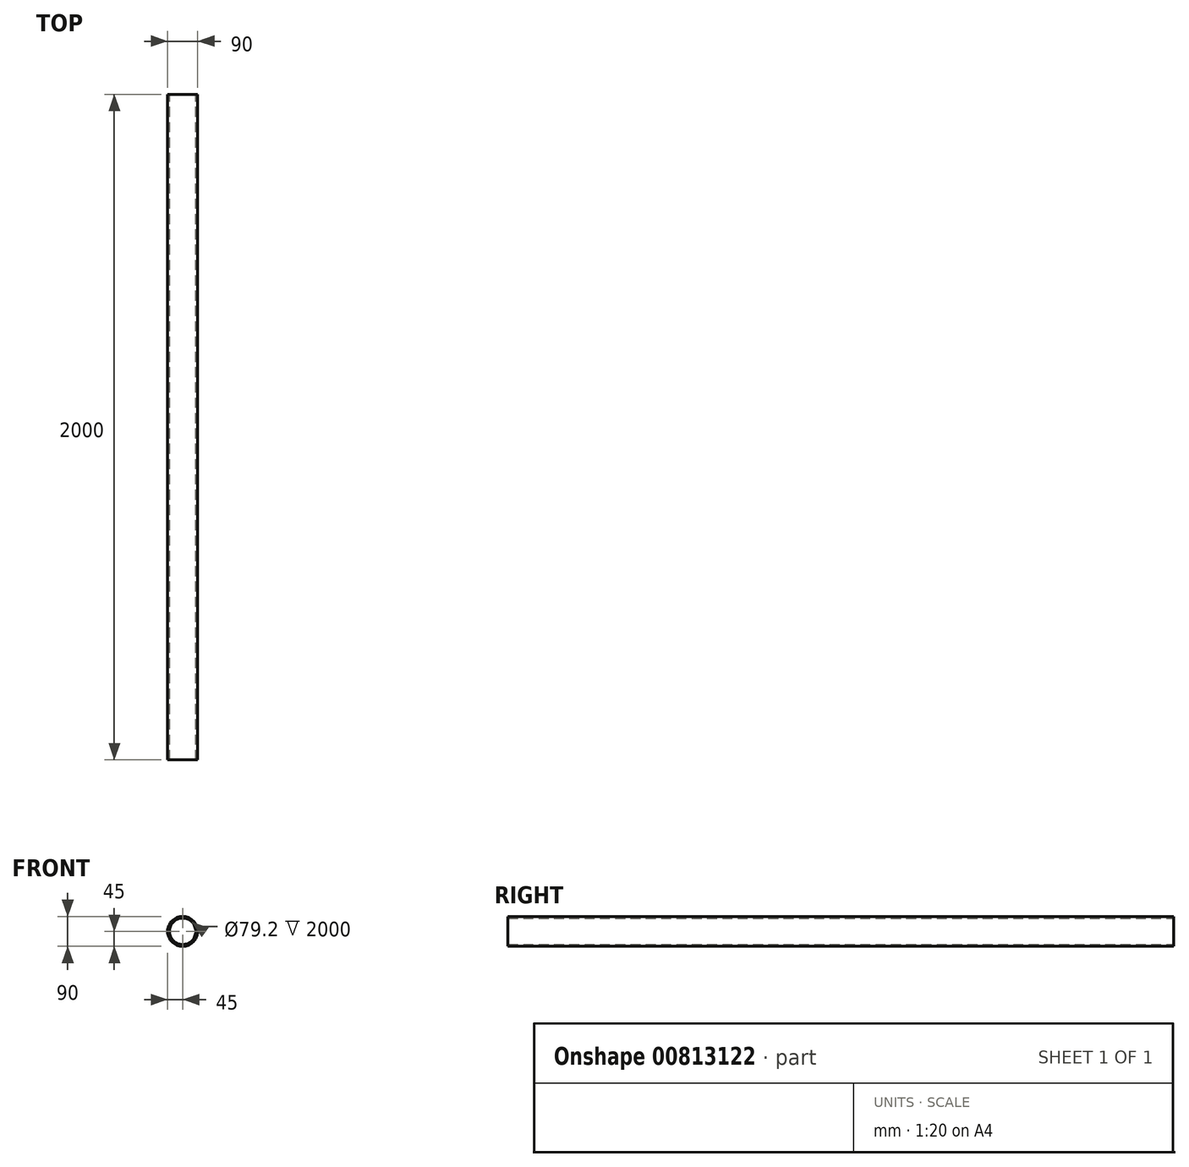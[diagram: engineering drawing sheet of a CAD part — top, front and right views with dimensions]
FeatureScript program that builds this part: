
annotation { "Feature Type Name" : "Feature", "Feature Type Description" : "" }
export const myFeature = defineFeature(function(context is Context, id is Id, definition is map)
    precondition{}
    {
        {
            var Q0;
            Q0=qCreatedBy(makeId("Front.planeOp"),FACE);
            var sketch = newSketch(context, id + "F0", { "sketchPlane" : qUnion([Q0])});
            skCircle(sketch, "E0", {"center": v(0, 0) * mm, "radius": 39.6 * mm});
            skCircle(sketch, "E1", {"center": v(0, 0) * mm, "radius": 45 * mm});
            skSolve(sketch);
        }
        {
            var Q0;
            Q0=makeQuery(id+"F0.imprint","IMPRINT",FACE,{"disambiguationData":[TD([[makeQuery(id+"F0.imprint","IMPRINT",EDGE,{"derivedFrom":sQuery(id+"F0.wireOp",EDGE,"E0")}),-1.0]])]});
            extrude(context, id + "F1", {"entities" : qUnion([Q0]), "endBound" : BoundingType.SYMMETRIC, "depth" : 2000 * mm, "offsetDistance" : 25 * mm});
        }
    });
